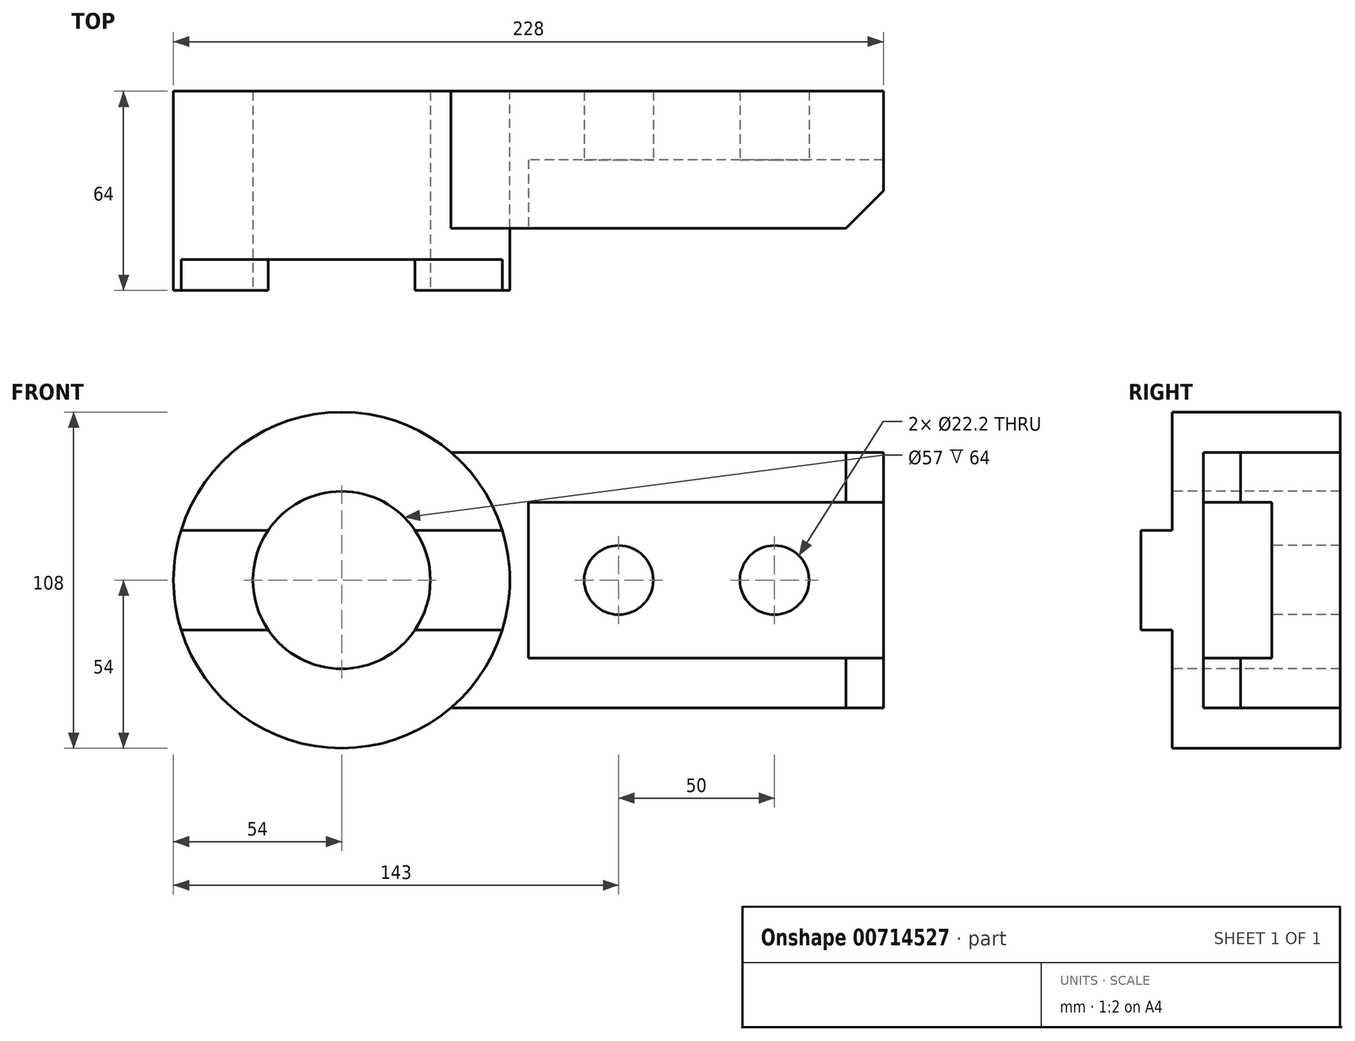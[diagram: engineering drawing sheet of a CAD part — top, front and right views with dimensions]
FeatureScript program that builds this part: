
annotation { "Feature Type Name" : "Feature", "Feature Type Description" : "" }
export const myFeature = defineFeature(function(context is Context, id is Id, definition is map)
    precondition{}
    {
        {
            var Q0;
            Q0=qCreatedBy(makeId("Front.planeOp"),FACE);
            var sketch = newSketch(context, id + "F0", { "sketchPlane" : qUnion([Q0])});
            skCircle(sketch, "E0", {"center": v(0, 0) * mm, "radius": 28.5 * mm});
            skCircle(sketch, "E1", {"center": v(0, 0) * mm, "radius": 54 * mm});
            skSolve(sketch);
        }
        {
            var Q0;
            Q0 = qSketchRegion(id + "F0", true);
            extrude(context, id + "F1", {"entities" : qUnion([Q0]), "oppositeDirection" : true, "depth" : 54 * mm, "offsetDistance" : 25 * mm});
        }
        {
            var Q0;
            Q0=qCreatedBy(makeId("Front.planeOp"),FACE);
            var sketch = newSketch(context, id + "F2", { "sketchPlane" : qUnion([Q0])});
            skLineSegment(sketch, "E2", {"start": v(-23.58, 16) * mm, "end": v(-51.58, 16) * mm});
            skLineSegment(sketch, "E3", {"start": v(-51.58, -16) * mm, "end": v(-23.58, -16) * mm});
            skLineSegment(sketch, "E4", {"start": v(23.58, 16) * mm, "end": v(51.58, 16) * mm});
            skLineSegment(sketch, "E5.trimOffspring", {"start": v(23.58, -16) * mm, "end": v(51.58, -16) * mm});
            skArc(sketch, "E6", {"start": v(-51.58, 16) * mm, "mid": v(-54, 0) * mm, "end": v(-51.58, -16) * mm});
            skArc(sketch, "E7", {"start": v(-23.58, 16) * mm, "mid": v(-28.5, 0) * mm, "end": v(-23.58, -16) * mm});
            skArc(sketch, "E8.trimOffspring", {"start": v(51.58, -16) * mm, "mid": v(54, 0) * mm, "end": v(51.58, 16) * mm});
            skArc(sketch, "E9.trimOffspring", {"start": v(23.58, -16) * mm, "mid": v(28.5, 0) * mm, "end": v(23.58, 16) * mm});
            skSolve(sketch);
        }
        {
            var Q0;
            Q0 = qSketchRegion(id + "F2", true);
            extrude(context, id + "F3", {"entities" : qUnion([Q0]), "operationType" : NewBodyOperationType.ADD, "depth" : 10 * mm, "offsetDistance" : 25 * mm});
        }
        {
            var Q0;
            Q0=makeQuery(id+"F1.opExtrude","CAP_FACE",FACE,{"disambiguationData":[OSD([sQuery(id+"F0.wireOp",EDGE,"E0"),sQuery(id+"F0.wireOp",EDGE,"E1")])],"isStart":false});
            var sketch = newSketch(context, id + "F4", { "sketchPlane" : qUnion([Q0])});
            skLineSegment(sketch, "E10", {"start": v(-174, 0) * mm, "end": v(-174, 41) * mm});
            skLineSegment(sketch, "E11", {"start": v(-174, 41) * mm, "end": v(-35.14, 41) * mm});
            skArc(sketch, "E12", {"start": v(-35.14, 41) * mm, "mid": v(-49.06, 22.56) * mm, "end": v(-54, 0) * mm});
            skLineSegment(sketch, "E13.MirrorCS", {"start": v(-174, -41) * mm, "end": v(-35.14, -41) * mm});
            skArc(sketch, "E14.MirrorCS", {"start": v(-35.14, -41) * mm, "mid": v(-49.06, -22.56) * mm, "end": v(-54, 0) * mm});
            skLineSegment(sketch, "E15.MirrorCS", {"start": v(-174, 0) * mm, "end": v(-174, -41) * mm});
            skSolve(sketch);
        }
        {
            var Q0;
            Q0 = qSketchRegion(id + "F4", true);
            extrude(context, id + "F5", {"entities" : qUnion([Q0]), "oppositeDirection" : true, "depth" : 44 * mm, "offsetDistance" : 25 * mm});
        }
        {
            var Q0;
            Q0=makeQuery(id+"F5.opExtrude","CAP_FACE",FACE,{"disambiguationData":[OSD([sQuery(id+"F4.wireOp",EDGE,"E10"),sQuery(id+"F4.wireOp",EDGE,"E11"),sQuery(id+"F4.wireOp",EDGE,"E12"),sQuery(id+"F4.wireOp",EDGE,"E13.MirrorCS"),sQuery(id+"F4.wireOp",EDGE,"E14.MirrorCS"),sQuery(id+"F4.wireOp",EDGE,"E15.MirrorCS")])],"isStart":false});
            var sketch = newSketch(context, id + "F6", { "sketchPlane" : qUnion([Q0])});
            skLineSegment(sketch, "E16", {"start": v(174, -25) * mm, "end": v(60, -25) * mm});
            skLineSegment(sketch, "E17", {"start": v(60, -25) * mm, "end": v(60, 25) * mm});
            skLineSegment(sketch, "E18", {"start": v(60, 25) * mm, "end": v(174, 25) * mm});
            skLineSegment(sketch, "E19", {"start": v(174, 25) * mm, "end": v(174, -25) * mm});
            skSolve(sketch);
        }
        {
            var Q0;
            Q0 = qSketchRegion(id + "F6", true);
            extrude(context, id + "F7", {"entities" : qUnion([Q0]), "operationType" : NewBodyOperationType.REMOVE, "oppositeDirection" : true, "depth" : 22 * mm, "offsetDistance" : 25 * mm});
        }
        {
            var Q0;
            {var subQ0=sQuery(id+"F4.wireOp",EDGE,"E15.MirrorCS");var subQ1=sQuery(id+"F4.wireOp",EDGE,"E11");var subQ2=sQuery(id+"F4.wireOp",EDGE,"E10");Q0=makeQuery(id+"F7.boolean.opBoolean","SPLIT",EDGE,{"disambiguationData":[TD([makeQuery(id+"F5.opExtrude","SWEPT_FACE",FACE,{"disambiguationData":[OSD([subQ1])]})])],"derivedFrom":makeQuery(id+"F5.opExtrude","CAP_EDGE",EDGE,{"disambiguationData":[OSD([subQ2,subQ0])],"isStart":false})});}
            var Q1;
            {var subQ0=sQuery(id+"F4.wireOp",EDGE,"E15.MirrorCS");var subQ1=sQuery(id+"F4.wireOp",EDGE,"E13.MirrorCS");var subQ2=sQuery(id+"F4.wireOp",EDGE,"E10");Q1=makeQuery(id+"F7.boolean.opBoolean","SPLIT",EDGE,{"disambiguationData":[TD([makeQuery(id+"F5.opExtrude","SWEPT_FACE",FACE,{"disambiguationData":[OSD([subQ1])]})])],"derivedFrom":makeQuery(id+"F5.opExtrude","CAP_EDGE",EDGE,{"disambiguationData":[OSD([subQ2,subQ0])],"isStart":false})});}
            chamfer(context, id + "F8", {"entities" : qUnion([Q0, Q1]), "width" : 12 * mm, "tangentPropagation" : true});
        }
        {
            var Q0;
            Q0=makeQuery(id+"F7.boolean.opBoolean","COPY",FACE,{"derivedFrom":makeQuery(id+"F7.opExtrude","CAP_FACE",FACE,{"disambiguationData":[OSD([sQuery(id+"F6.wireOp",EDGE,"E16"),sQuery(id+"F6.wireOp",EDGE,"E17"),sQuery(id+"F6.wireOp",EDGE,"E18"),sQuery(id+"F6.wireOp",EDGE,"E19")])],"isStart":false})});
            var sketch = newSketch(context, id + "F9", { "sketchPlane" : qUnion([Q0])});
            skCircle(sketch, "E20", {"center": v(139, 0) * mm, "radius": 11.1 * mm});
            skCircle(sketch, "E21", {"center": v(89, 0) * mm, "radius": 11.1 * mm});
            skSolve(sketch);
        }
        {
            var Q0;
            Q0 = qSketchRegion(id + "F9", true);
            extrude(context, id + "F10", {"entities" : qUnion([Q0]), "operationType" : NewBodyOperationType.REMOVE, "endBound" : BoundingType.UP_TO_NEXT, "oppositeDirection" : true, "depth" : 25 * mm, "offsetDistance" : 25 * mm});
        }
    });
